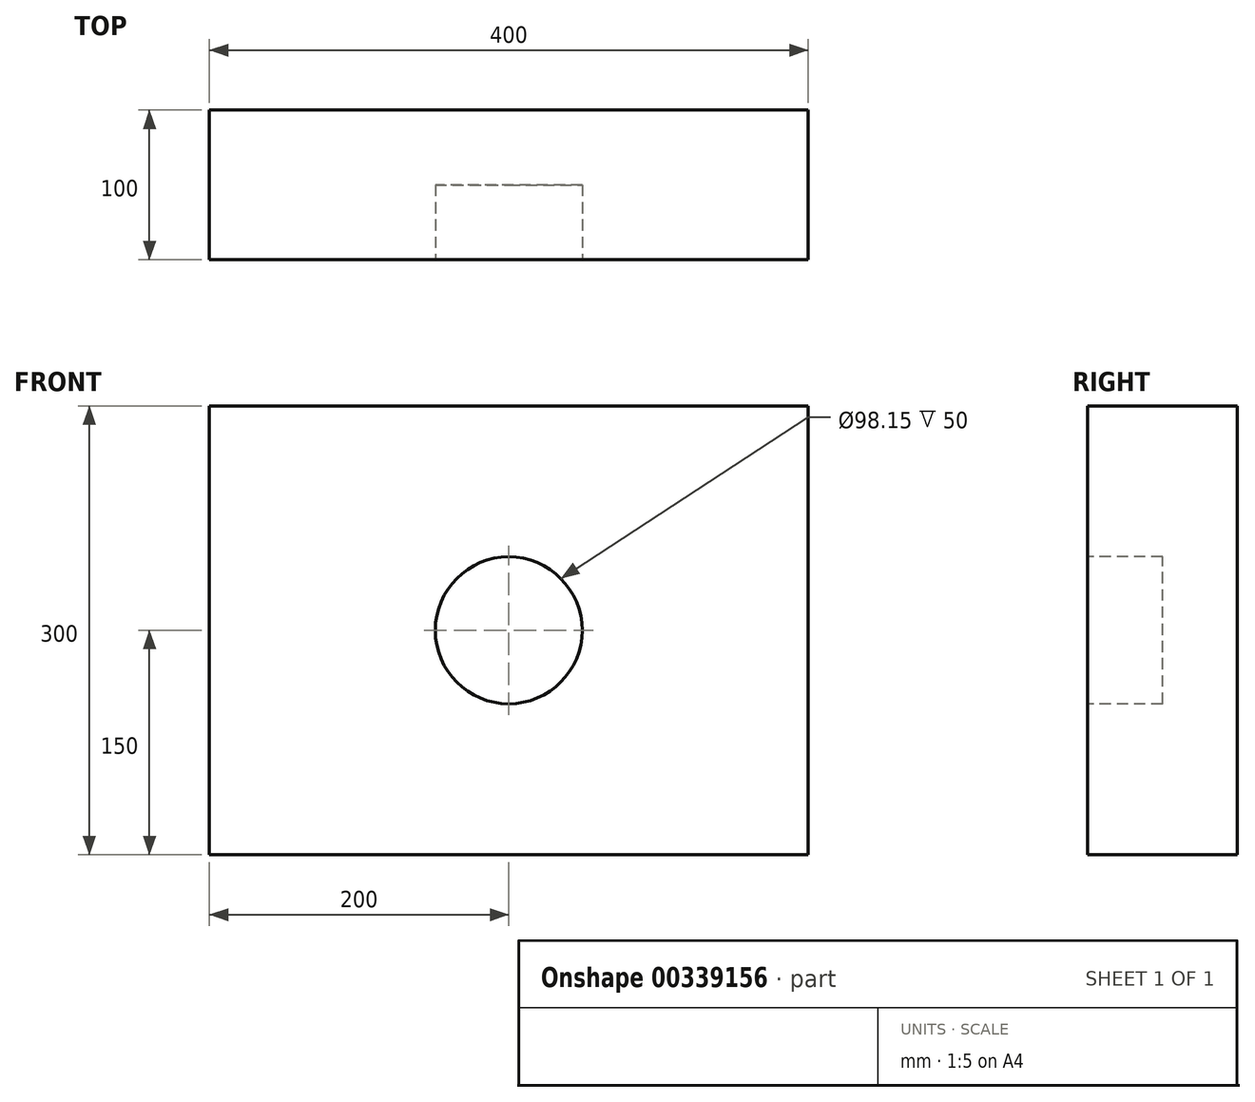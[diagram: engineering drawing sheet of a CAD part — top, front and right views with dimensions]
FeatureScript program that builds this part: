
annotation { "Feature Type Name" : "Feature", "Feature Type Description" : "" }
export const myFeature = defineFeature(function(context is Context, id is Id, definition is map)
    precondition{}
    {
        {
            var Q0;
            Q0=qCreatedBy(makeId("Front.planeOp"),FACE);
            var sketch = newSketch(context, id + "F0", { "sketchPlane" : qUnion([Q0])});
            skLineSegment(sketch, "E0.bottom", {"start": v(200, 150) * mm, "end": v(-200, 150) * mm});
            skLineSegment(sketch, "E0.top", {"start": v(200, -150) * mm, "end": v(-200, -150) * mm});
            skLineSegment(sketch, "E0.left", {"start": v(200, 150) * mm, "end": v(200, -150) * mm});
            skLineSegment(sketch, "E0.right", {"start": v(-200, 150) * mm, "end": v(-200, -150) * mm});
            skPoint(sketch, "E0.middle", {"position": v(0, 0) * mm});
            skLineSegment(sketch, "E1.bottom", {"start": v(-200, 50) * mm, "end": v(-120, 50) * mm});
            skLineSegment(sketch, "E1.top", {"start": v(-200, -50) * mm, "end": v(-120, -50) * mm});
            skLineSegment(sketch, "E1.right", {"start": v(-120, 50) * mm, "end": v(-120, -50) * mm});
            skPoint(sketch, "E1.middle", {"position": v(-200, 0) * mm});
            skLineSegment(sketch, "E2.bottom", {"start": v(200, 55.59) * mm, "end": v(175, 55.59) * mm});
            skLineSegment(sketch, "E2.top", {"start": v(200, -55.59) * mm, "end": v(175, -55.59) * mm});
            skLineSegment(sketch, "E2.right", {"start": v(175, 55.59) * mm, "end": v(175, -55.59) * mm});
            skPoint(sketch, "E2.middle", {"position": v(200, 0) * mm});
            skPoint(sketch, "E1.left.start.orphan", {"position": v(-280, 50) * mm});
            skPoint(sketch, "E3.orphan", {"position": v(-280, -50) * mm});
            skPoint(sketch, "E2.left.start.orphan", {"position": v(225, 55.59) * mm});
            skPoint(sketch, "E4.orphan", {"position": v(225, -55.59) * mm});
            skSolve(sketch);
        }
        {
            var Q0;
            Q0 = qSketchRegion(id + "F0", true);
            extrude(context, id + "F1", {"entities" : qUnion([Q0]), "depth" : 100 * mm});
        }
        {
            var Q0;
            Q0=makeQuery(id+"F1.opExtrude","CAP_FACE",FACE,{"disambiguationData":[OSD([sQuery(id+"F0.wireOp",EDGE,"E0.bottom"),sQuery(id+"F0.wireOp",EDGE,"E0.top"),sQuery(id+"F0.wireOp",EDGE,"E0.left"),sQuery(id+"F0.wireOp",EDGE,"E0.right")])],"isStart":false});
            var sketch = newSketch(context, id + "F2", { "sketchPlane" : qUnion([Q0])});
            skCircle(sketch, "E5", {"center": v(0, 0) * mm, "radius": 49.07 * mm});
            skSolve(sketch);
        }
        {
            var Q0;
            Q0 = qSketchRegion(id + "F2", true);
            extrude(context, id + "F3", {"entities" : qUnion([Q0]), "operationType" : NewBodyOperationType.REMOVE, "oppositeDirection" : true, "depth" : 50 * mm});
        }
    });
